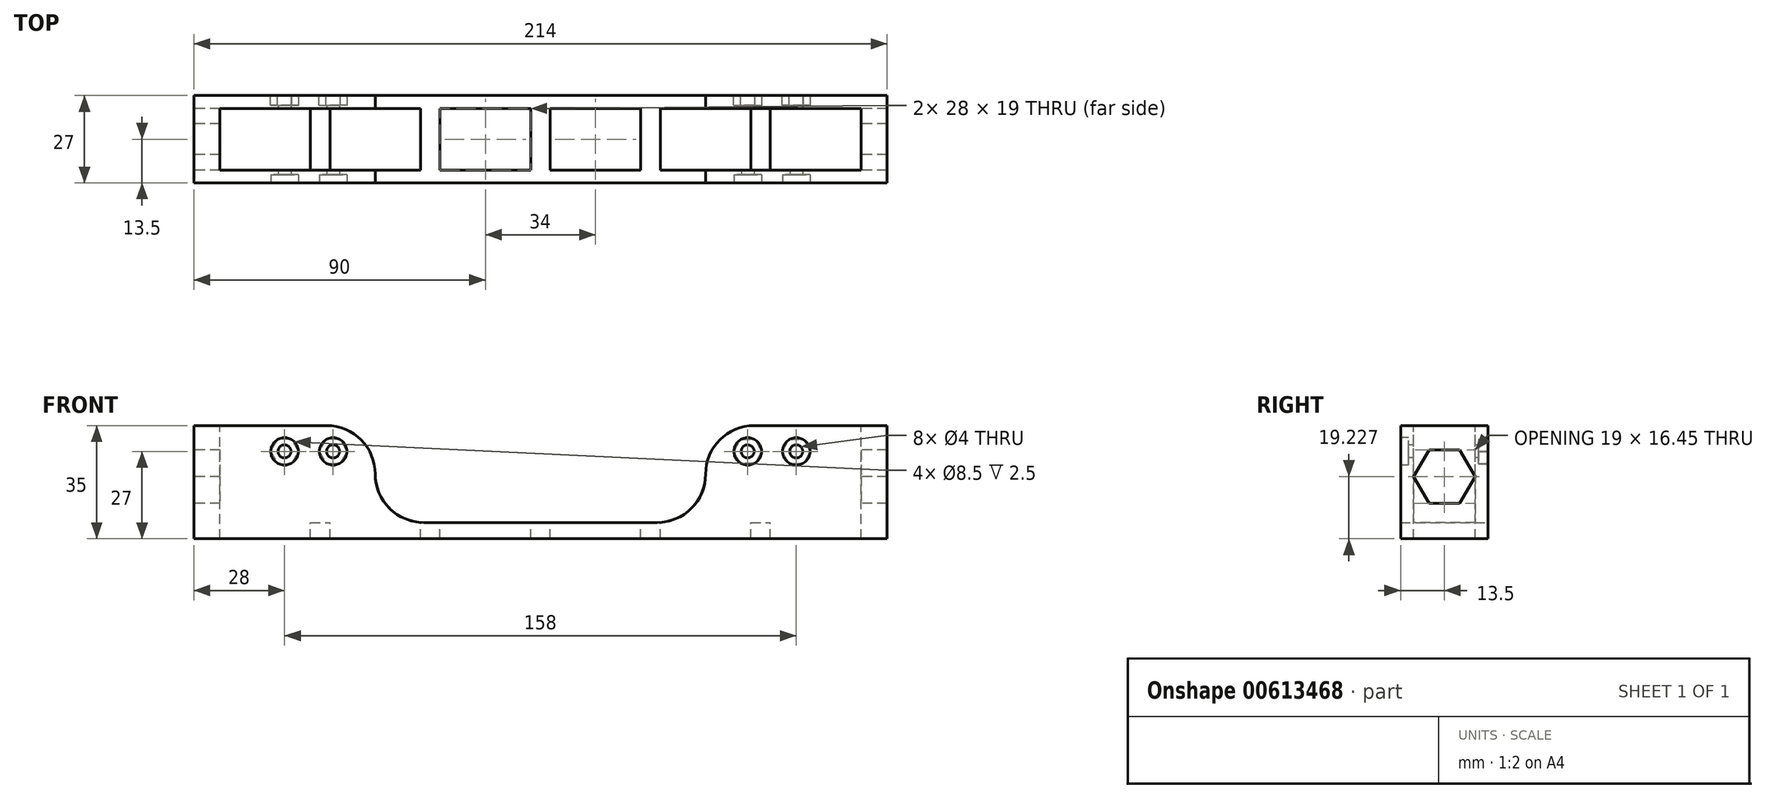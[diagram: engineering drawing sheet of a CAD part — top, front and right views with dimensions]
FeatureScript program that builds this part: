
annotation { "Feature Type Name" : "Feature", "Feature Type Description" : "" }
export const myFeature = defineFeature(function(context is Context, id is Id, definition is map)
    precondition{}
    {
        {
            var Q0;
            Q0=qCreatedBy(makeId("Top.planeOp"),FACE);
            var sketch = newSketch(context, id + "F0", { "sketchPlane" : qUnion([Q0])});
            skLineSegment(sketch, "E0.bottom", {"start": v(-107, -13.5) * mm, "end": v(107, -13.5) * mm});
            skLineSegment(sketch, "E0.top", {"start": v(-107, 13.5) * mm, "end": v(107, 13.5) * mm});
            skLineSegment(sketch, "E0.left", {"start": v(-107, -13.5) * mm, "end": v(-107, 13.5) * mm});
            skLineSegment(sketch, "E0.right", {"start": v(107, -13.5) * mm, "end": v(107, 13.5) * mm});
            skPoint(sketch, "E0.middle", {"position": v(0, 0) * mm});
            skLineSegment(sketch, "E1.bottom", {"start": v(-99, 9.5) * mm, "end": v(-71, 9.5) * mm});
            skLineSegment(sketch, "E1.top", {"start": v(-99, -9.5) * mm, "end": v(-71, -9.5) * mm});
            skLineSegment(sketch, "E1.left", {"start": v(-99, 9.5) * mm, "end": v(-99, -9.5) * mm});
            skLineSegment(sketch, "E1.right", {"start": v(-71, 9.5) * mm, "end": v(-71, -9.5) * mm});
            skLineSegment(sketch, "E2.1.0.0", {"start": v(-37, 9.5) * mm, "end": v(-37, -9.5) * mm});
            skLineSegment(sketch, "E2.1.0.1", {"start": v(-65, 9.5) * mm, "end": v(-37, 9.5) * mm});
            skLineSegment(sketch, "E2.1.0.2", {"start": v(-65, 9.5) * mm, "end": v(-65, -9.5) * mm});
            skLineSegment(sketch, "E2.1.0.3", {"start": v(-65, -9.5) * mm, "end": v(-37, -9.5) * mm});
            skLineSegment(sketch, "E2.2.0.0", {"start": v(-3, 9.5) * mm, "end": v(-3, -9.5) * mm});
            skLineSegment(sketch, "E2.2.0.1", {"start": v(-31, 9.5) * mm, "end": v(-3, 9.5) * mm});
            skLineSegment(sketch, "E2.2.0.2", {"start": v(-31, 9.5) * mm, "end": v(-31, -9.5) * mm});
            skLineSegment(sketch, "E2.2.0.3", {"start": v(-31, -9.5) * mm, "end": v(-3, -9.5) * mm});
            skLineSegment(sketch, "E2.direction1", {"start": v(-71, -9.5) * mm, "end": v(-37, -9.5) * mm, "construction": true});
            skLineSegment(sketch, "E3.0.3.0", {"start": v(31, 9.5) * mm, "end": v(31, -9.5) * mm});
            skLineSegment(sketch, "E3.3.3.0", {"start": v(3, 9.5) * mm, "end": v(31, 9.5) * mm});
            skLineSegment(sketch, "E3.6.3.0", {"start": v(3, 9.5) * mm, "end": v(3, -9.5) * mm});
            skLineSegment(sketch, "E3.9.3.0", {"start": v(3, -9.5) * mm, "end": v(31, -9.5) * mm});
            skLineSegment(sketch, "E3.0.4.0", {"start": v(65, 9.5) * mm, "end": v(65, -9.5) * mm});
            skLineSegment(sketch, "E3.3.4.0", {"start": v(37, 9.5) * mm, "end": v(65, 9.5) * mm});
            skLineSegment(sketch, "E3.6.4.0", {"start": v(37, 9.5) * mm, "end": v(37, -9.5) * mm});
            skLineSegment(sketch, "E3.9.4.0", {"start": v(37, -9.5) * mm, "end": v(65, -9.5) * mm});
            skLineSegment(sketch, "E3.0.5.0", {"start": v(99, 9.5) * mm, "end": v(99, -9.5) * mm});
            skLineSegment(sketch, "E3.3.5.0", {"start": v(71, 9.5) * mm, "end": v(99, 9.5) * mm});
            skLineSegment(sketch, "E3.6.5.0", {"start": v(71, 9.5) * mm, "end": v(71, -9.5) * mm});
            skLineSegment(sketch, "E3.9.5.0", {"start": v(71, -9.5) * mm, "end": v(99, -9.5) * mm});
            skLineSegment(sketch, "E4", {"start": v(-51, 9.5) * mm, "end": v(-51, 13.5) * mm});
            skLineSegment(sketch, "E5", {"start": v(-51, -9.5) * mm, "end": v(-51, -13.5) * mm});
            skLineSegment(sketch, "E6.MirrorCS", {"start": v(51, 9.5) * mm, "end": v(51, 13.5) * mm});
            skLineSegment(sketch, "E7.MirrorCS", {"start": v(51, -9.5) * mm, "end": v(51, -13.5) * mm});
            skLineSegment(sketch, "E8", {"start": v(-65, 9.5) * mm, "end": v(-71, 9.5) * mm});
            skLineSegment(sketch, "E9", {"start": v(-71, -9.5) * mm, "end": v(-65, -9.5) * mm});
            skLineSegment(sketch, "E10.MirrorCS", {"start": v(65, 9.5) * mm, "end": v(71, 9.5) * mm});
            skLineSegment(sketch, "E11.MirrorCS", {"start": v(71, -9.5) * mm, "end": v(65, -9.5) * mm});
            skSolve(sketch);
        }
        {
            var Q0;
            Q0 = qSketchRegion(id + "F0", true);
            var Q1;
            Q1=makeQuery(id+"F0.imprint","IMPRINT",FACE,{"disambiguationData":[TD([[makeQuery(id+"F0.imprint","IMPRINT",EDGE,{"derivedFrom":sQuery(id+"F0.wireOp",EDGE,"E1.right")}),1.0]])]});
            var Q2;
            Q2=makeQuery(id+"F0.imprint","IMPRINT",FACE,{"disambiguationData":[TD([[makeQuery(id+"F0.imprint","IMPRINT",EDGE,{"derivedFrom":sQuery(id+"F0.wireOp",EDGE,"E3.0.4.0")}),1.0]])]});
            extrude(context, id + "F1", {"entities" : qUnion([Q0, Q1, Q2]), "oppositeDirection" : true, "depth" : 5 * mm, "offsetDistance" : 25 * mm});
        }
        {
            var Q0;
            {var subQ0=sQuery(id+"F0.wireOp",EDGE,"E0.right");Q0=makeQuery(id+"F0.imprint","IMPRINT",FACE,{"disambiguationData":[TD([[makeQuery(id+"F0.imprint","IMPRINT",EDGE,{"derivedFrom":subQ0}),1.0]])]});}
            var Q1;
            {var subQ2=sQuery(id+"F0.wireOp",EDGE,"E0.left");Q1=makeQuery(id+"F0.imprint","IMPRINT",FACE,{"disambiguationData":[TD([[makeQuery(id+"F0.imprint","IMPRINT",EDGE,{"derivedFrom":subQ2}),-1.0]])]});}
            extrude(context, id + "F2", {"entities" : qUnion([Q0, Q1]), "operationType" : NewBodyOperationType.ADD, "depth" : 30 * mm, "offsetDistance" : 25 * mm});
        }
        {
            var Q0;
            Q0=makeQuery(id+"F2.opExtrude","CAP_EDGE",EDGE,{"disambiguationData":[OSD([sQuery(id+"F0.wireOp",EDGE,"E6.MirrorCS")])],"isStart":true});
            var Q1;
            Q1=makeQuery(id+"F2.opExtrude","CAP_EDGE",EDGE,{"disambiguationData":[OSD([sQuery(id+"F0.wireOp",EDGE,"E6.MirrorCS")])],"isStart":false});
            var Q2;
            Q2=makeQuery(id+"F2.opExtrude","CAP_EDGE",EDGE,{"disambiguationData":[OSD([sQuery(id+"F0.wireOp",EDGE,"E4")])],"isStart":false});
            var Q3;
            Q3=makeQuery(id+"F2.opExtrude","CAP_EDGE",EDGE,{"disambiguationData":[OSD([sQuery(id+"F0.wireOp",EDGE,"E4")])],"isStart":true});
            var Q4;
            Q4=makeQuery(id+"F2.opExtrude","CAP_EDGE",EDGE,{"disambiguationData":[OSD([sQuery(id+"F0.wireOp",EDGE,"E5")])],"isStart":false});
            var Q5;
            Q5=makeQuery(id+"F2.opExtrude","CAP_EDGE",EDGE,{"disambiguationData":[OSD([sQuery(id+"F0.wireOp",EDGE,"E7.MirrorCS")])],"isStart":false});
            fillet(context, id + "F3", {"entities" : qUnion([Q0, Q1, Q2, Q3, Q4, Q5]), "radius" : 15 * mm, "allowEdgeOverflow" : false});
        }
        {
            var Q0;
            Q0=qCreatedBy(makeId("Front.planeOp"),FACE);
            var sketch = newSketch(context, id + "F4", { "sketchPlane" : qUnion([Q0])});
            skCircle(sketch, "E12", {"center": v(0, 105.57) * mm, "radius": 100 * mm});
            skCircle(sketch, "E13", {"center": v(-79, 22) * mm, "radius": 15 * mm});
            skCircle(sketch, "E14", {"center": v(-79, 22) * mm, "radius": 18 * mm});
            skSolve(sketch);
        }
        {
            var Q0;
            {var subQ0=sQuery(id+"F0.wireOp",EDGE,"E0.bottom");Q0=makeQuery(id+"F2.boolean.opBoolean","MERGE",FACE,{"derivedFrom":[makeQuery(id+"F1.opExtrude","SWEPT_FACE",FACE,{"disambiguationData":[OSD([subQ0])]}),makeQuery(id+"F2.opExtrude","SWEPT_FACE",FACE,{"disambiguationData":[OSD([subQ0]),TDD([makeQuery(id+"F0.imprint","IMPRINT",EDGE,{"disambiguationData":[TD([[makeQuery(id+"F0.imprint","INTERSECT",VERTEX,{"derivedFrom":[subQ0,sQuery(id+"F0.wireOp",EDGE,"E0.left")]}),-1.0]])],"derivedFrom":subQ0})])]}),makeQuery(id+"F2.opExtrude","SWEPT_FACE",FACE,{"disambiguationData":[OSD([subQ0]),TDD([makeQuery(id+"F0.imprint","IMPRINT",EDGE,{"disambiguationData":[TD([[makeQuery(id+"F0.imprint","INTERSECT",VERTEX,{"derivedFrom":[subQ0,sQuery(id+"F0.wireOp",EDGE,"E0.right")]}),1.0]])],"derivedFrom":subQ0})])]})]});}
            var sketch = newSketch(context, id + "F5", { "sketchPlane" : qUnion([Q0])});
            skPoint(sketch, "E15.0", {"position": v(-79, 22) * mm});
            skPoint(sketch, "E16.MirrorP", {"position": v(79, 22) * mm});
            skPoint(sketch, "E17", {"position": v(-64, 22) * mm});
            skPoint(sketch, "E18.MirrorP", {"position": v(64, 22) * mm});
            skSolve(sketch);
        }
        {
            var Q0;
            Q0=sQuery(id+"F5.wireOp",VERTEX,"E15.0");
            var Q1;
            Q1=sQuery(id+"F5.wireOp",VERTEX,"E16.MirrorP");
            var Q2;
            Q2=sQuery(id+"F5.wireOp",VERTEX,"E17");
            var Q3;
            Q3=sQuery(id+"F5.wireOp",VERTEX,"E18.MirrorP");
            var Q4;
            Q4=makeQuery(id+"F1.opExtrude","SWEPT_BODY",BODY,{"disambiguationData":[OSD([sQuery(id+"F0.wireOp",EDGE,"E0.bottom"),sQuery(id+"F0.wireOp",EDGE,"E0.top"),sQuery(id+"F0.wireOp",EDGE,"E0.left"),sQuery(id+"F0.wireOp",EDGE,"E0.right"),sQuery(id+"F0.wireOp",EDGE,"E1.bottom"),sQuery(id+"F0.wireOp",EDGE,"E1.top"),sQuery(id+"F0.wireOp",EDGE,"E1.left"),sQuery(id+"F0.wireOp",EDGE,"E1.right"),sQuery(id+"F0.wireOp",EDGE,"E2.1.0.0"),sQuery(id+"F0.wireOp",EDGE,"E2.1.0.1"),sQuery(id+"F0.wireOp",EDGE,"E2.1.0.2"),sQuery(id+"F0.wireOp",EDGE,"E2.1.0.3"),sQuery(id+"F0.wireOp",EDGE,"E2.2.0.0"),sQuery(id+"F0.wireOp",EDGE,"E2.2.0.1"),sQuery(id+"F0.wireOp",EDGE,"E2.2.0.2"),sQuery(id+"F0.wireOp",EDGE,"E2.2.0.3"),sQuery(id+"F0.wireOp",EDGE,"E3.0.3.0"),sQuery(id+"F0.wireOp",EDGE,"E3.3.3.0"),sQuery(id+"F0.wireOp",EDGE,"E3.6.3.0"),sQuery(id+"F0.wireOp",EDGE,"E3.9.3.0"),sQuery(id+"F0.wireOp",EDGE,"E3.0.4.0"),sQuery(id+"F0.wireOp",EDGE,"E3.3.4.0"),sQuery(id+"F0.wireOp",EDGE,"E3.6.4.0"),sQuery(id+"F0.wireOp",EDGE,"E3.9.4.0"),sQuery(id+"F0.wireOp",EDGE,"E3.0.5.0"),sQuery(id+"F0.wireOp",EDGE,"E3.3.5.0"),sQuery(id+"F0.wireOp",EDGE,"E3.6.5.0"),sQuery(id+"F0.wireOp",EDGE,"E3.9.5.0")])]});
            hole(context, id + "F6", {"style" : HoleStyle.C_BORE, "endStyle" : HoleEndStyle.THROUGH, "holeDiameter" : 4 * mm, "cBoreDiameter" : 8.5 * mm, "cBoreDepth" : 2.5 * mm, "majorDiameter" : 5 * mm, "isTappedThrough" : true, "tappedDepth" : 6 * mm, "tapClearance" : 3, "locations" : qUnion([Q0, Q1, Q2, Q3]), "scope" : qUnion([Q4])});
        }
        {
            var Q0;
            {var subQ0=sQuery(id+"F0.wireOp",EDGE,"E0.top");Q0=makeQuery(id+"F2.boolean.opBoolean","MERGE",FACE,{"derivedFrom":[makeQuery(id+"F1.opExtrude","SWEPT_FACE",FACE,{"disambiguationData":[OSD([subQ0])]}),makeQuery(id+"F2.opExtrude","SWEPT_FACE",FACE,{"disambiguationData":[OSD([subQ0]),TDD([makeQuery(id+"F0.imprint","IMPRINT",EDGE,{"disambiguationData":[TD([[makeQuery(id+"F0.imprint","INTERSECT",VERTEX,{"derivedFrom":[subQ0,sQuery(id+"F0.wireOp",EDGE,"E0.left")]}),-1.0]])],"derivedFrom":subQ0})])]}),makeQuery(id+"F2.opExtrude","SWEPT_FACE",FACE,{"disambiguationData":[OSD([subQ0]),TDD([makeQuery(id+"F0.imprint","IMPRINT",EDGE,{"disambiguationData":[TD([[makeQuery(id+"F0.imprint","INTERSECT",VERTEX,{"derivedFrom":[subQ0,sQuery(id+"F0.wireOp",EDGE,"E0.right")]}),1.0]])],"derivedFrom":subQ0})])]})]});}
            var sketch = newSketch(context, id + "F7", { "sketchPlane" : qUnion([Q0])});
            skCircle(sketch, "E19.cCircle", {"center": v(79, 22) * mm, "radius": 3.8 * mm, "construction": true});
            skLineSegment(sketch, "E19.0", {"start": v(81.17, 18.18) * mm, "end": v(76.78, 18.22) * mm});
            skLineSegment(sketch, "E19.1", {"start": v(76.78, 18.22) * mm, "end": v(74.61, 22.03) * mm});
            skLineSegment(sketch, "E19.2", {"start": v(74.61, 22.03) * mm, "end": v(76.83, 25.82) * mm});
            skLineSegment(sketch, "E19.3", {"start": v(76.83, 25.82) * mm, "end": v(81.22, 25.78) * mm});
            skLineSegment(sketch, "E19.4", {"start": v(81.22, 25.78) * mm, "end": v(83.39, 21.97) * mm});
            skLineSegment(sketch, "E19.5", {"start": v(83.39, 21.97) * mm, "end": v(81.17, 18.18) * mm});
            skPoint(sketch, "E19.0.midPoint", {"position": v(78.97, 18.2) * mm});
            skLineSegment(sketch, "E20.MirrorCS", {"start": v(-76.78, 18.22) * mm, "end": v(-74.61, 22.03) * mm});
            skLineSegment(sketch, "E21.MirrorCS", {"start": v(-81.17, 18.18) * mm, "end": v(-76.78, 18.22) * mm});
            skLineSegment(sketch, "E22.MirrorCS", {"start": v(-83.39, 21.97) * mm, "end": v(-81.17, 18.18) * mm});
            skLineSegment(sketch, "E23.MirrorCS", {"start": v(-81.22, 25.78) * mm, "end": v(-83.39, 21.97) * mm});
            skLineSegment(sketch, "E24.MirrorCS", {"start": v(-76.83, 25.82) * mm, "end": v(-81.22, 25.78) * mm});
            skLineSegment(sketch, "E25.MirrorCS", {"start": v(-74.61, 22.03) * mm, "end": v(-76.83, 25.82) * mm});
            skCircle(sketch, "E26.cCircle", {"center": v(64, 22) * mm, "radius": 3.8 * mm, "construction": true});
            skLineSegment(sketch, "E26.0", {"start": v(66.2, 18.2) * mm, "end": v(61.8, 18.2) * mm});
            skLineSegment(sketch, "E26.1", {"start": v(61.8, 18.2) * mm, "end": v(59.61, 22) * mm});
            skLineSegment(sketch, "E26.2", {"start": v(59.61, 22) * mm, "end": v(61.8, 25.8) * mm});
            skLineSegment(sketch, "E26.3", {"start": v(61.8, 25.8) * mm, "end": v(66.2, 25.8) * mm});
            skLineSegment(sketch, "E26.4", {"start": v(66.2, 25.8) * mm, "end": v(68.39, 22) * mm});
            skLineSegment(sketch, "E26.5", {"start": v(68.39, 22) * mm, "end": v(66.2, 18.2) * mm});
            skPoint(sketch, "E26.0.midPoint", {"position": v(64, 18.2) * mm});
            skLineSegment(sketch, "E27.MirrorCS", {"start": v(-61.8, 25.8) * mm, "end": v(-66.2, 25.8) * mm});
            skLineSegment(sketch, "E28.MirrorCS", {"start": v(-66.2, 25.8) * mm, "end": v(-68.39, 22) * mm});
            skLineSegment(sketch, "E29.MirrorCS", {"start": v(-68.39, 22) * mm, "end": v(-66.2, 18.2) * mm});
            skLineSegment(sketch, "E30.MirrorCS", {"start": v(-66.2, 18.2) * mm, "end": v(-61.8, 18.2) * mm});
            skLineSegment(sketch, "E31.MirrorCS", {"start": v(-61.8, 18.2) * mm, "end": v(-59.61, 22) * mm});
            skLineSegment(sketch, "E32.MirrorCS", {"start": v(-59.61, 22) * mm, "end": v(-61.8, 25.8) * mm});
            skSolve(sketch);
        }
        {
            var Q0;
            Q0=makeQuery(id+"F7.imprint","IMPRINT",FACE,{"disambiguationData":[TD([[makeQuery(id+"F7.imprint","IMPRINT",EDGE,{"derivedFrom":sQuery(id+"F7.wireOp",EDGE,"E20.MirrorCS")}),1.0]])]});
            var Q1;
            Q1=makeQuery(id+"F7.imprint","IMPRINT",FACE,{"disambiguationData":[TD([[makeQuery(id+"F7.imprint","IMPRINT",EDGE,{"derivedFrom":sQuery(id+"F7.wireOp",EDGE,"E27.MirrorCS")}),1.0]])]});
            var Q2;
            Q2=makeQuery(id+"F7.imprint","IMPRINT",FACE,{"disambiguationData":[TD([[makeQuery(id+"F7.imprint","IMPRINT",EDGE,{"derivedFrom":sQuery(id+"F7.wireOp",EDGE,"E26.0")}),-1.0]])]});
            var Q3;
            Q3=makeQuery(id+"F7.imprint","IMPRINT",FACE,{"disambiguationData":[TD([[makeQuery(id+"F7.imprint","IMPRINT",EDGE,{"derivedFrom":sQuery(id+"F7.wireOp",EDGE,"E19.0")}),-1.0]])]});
            extrude(context, id + "F8", {"entities" : qUnion([Q0, Q1, Q2, Q3]), "operationType" : NewBodyOperationType.REMOVE, "oppositeDirection" : true, "depth" : 3 * mm, "offsetDistance" : 25 * mm});
        }
        {
            var Q0;
            {var subQ0=sQuery(id+"F0.wireOp",EDGE,"E0.left");Q0=makeQuery(id+"F2.boolean.opBoolean","MERGE",FACE,{"derivedFrom":[makeQuery(id+"F1.opExtrude","SWEPT_FACE",FACE,{"disambiguationData":[OSD([subQ0])]}),makeQuery(id+"F2.opExtrude","SWEPT_FACE",FACE,{"disambiguationData":[OSD([subQ0])]})]});}
            var sketch = newSketch(context, id + "F9", { "sketchPlane" : qUnion([Q0])});
            skCircle(sketch, "E33.cCircle", {"center": v(0, 14.23) * mm, "radius": 8.23 * mm, "construction": true});
            skLineSegment(sketch, "E33.0", {"start": v(4.75, 6) * mm, "end": v(-4.75, 6) * mm});
            skLineSegment(sketch, "E33.1", {"start": v(-4.75, 6) * mm, "end": v(-9.5, 14.23) * mm});
            skLineSegment(sketch, "E33.2", {"start": v(-9.5, 14.23) * mm, "end": v(-4.75, 22.45) * mm});
            skLineSegment(sketch, "E33.3", {"start": v(-4.75, 22.45) * mm, "end": v(4.75, 22.45) * mm});
            skLineSegment(sketch, "E33.4", {"start": v(4.75, 22.45) * mm, "end": v(9.5, 14.23) * mm});
            skLineSegment(sketch, "E33.5", {"start": v(9.5, 14.23) * mm, "end": v(4.75, 6) * mm});
            skPoint(sketch, "E33.0.midPoint", {"position": v(0, 6) * mm});
            skSolve(sketch);
        }
        {
            var Q0;
            Q0=makeQuery(id+"F9.imprint","IMPRINT",FACE,{"disambiguationData":[TD([[makeQuery(id+"F9.imprint","IMPRINT",EDGE,{"derivedFrom":sQuery(id+"F9.wireOp",EDGE,"E33.0")}),-1.0]])]});
            var Q1;
            Q1=makeQuery(id+"F9.imprint","IMPRINT",FACE,{"disambiguationData":[TD([[makeQuery(id+"F9.imprint","IMPRINT",EDGE,{"derivedFrom":sQuery(id+"F9.wireOp",EDGE,"ec507e0f-55d1-4d31-adb5-030bde92c7bd.0")}),-1.0]])]});
            extrude(context, id + "F10", {"entities" : qUnion([Q0, Q1]), "operationType" : NewBodyOperationType.REMOVE, "endBound" : BoundingType.THROUGH_ALL, "oppositeDirection" : true, "depth" : 25 * mm, "offsetDistance" : 25 * mm});
        }
    });
